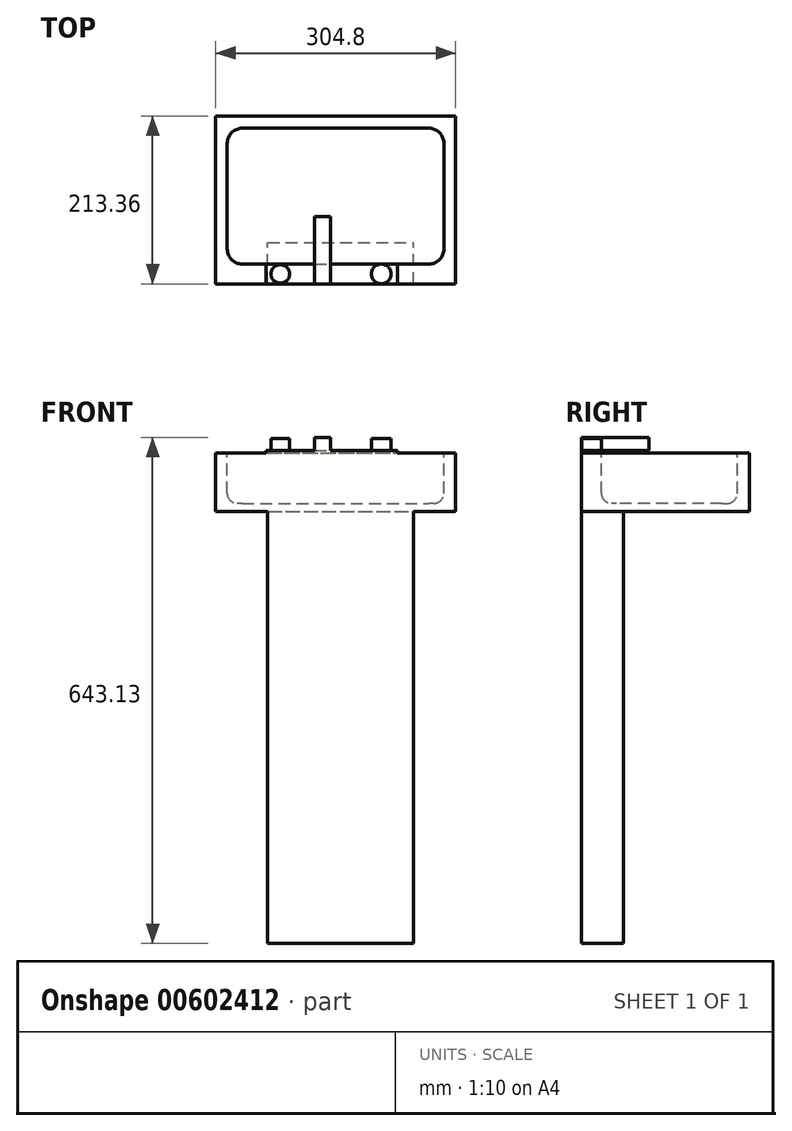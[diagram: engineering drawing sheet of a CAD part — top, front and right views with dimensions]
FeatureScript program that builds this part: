
annotation { "Feature Type Name" : "Feature", "Feature Type Description" : "" }
export const myFeature = defineFeature(function(context is Context, id is Id, definition is map)
    precondition{}
    {
        {
            var Q0;
            Q0=qCreatedBy(makeId("Top.planeOp"),FACE);
            var sketch = newSketch(context, id + "F0", { "sketchPlane" : qUnion([Q0])});
            skLineSegment(sketch, "E0.bottom", {"start": v(0, 0) * mm, "end": v(304.8, 0) * mm});
            skLineSegment(sketch, "E0.top", {"start": v(0, -213.36) * mm, "end": v(304.8, -213.36) * mm});
            skLineSegment(sketch, "E0.left", {"start": v(0, 0) * mm, "end": v(0, -213.36) * mm});
            skLineSegment(sketch, "E0.right", {"start": v(304.8, 0) * mm, "end": v(304.8, -213.36) * mm});
            skSolve(sketch);
        }
        {
            var Q0;
            Q0=makeQuery(id+"F0.imprint","IMPRINT",FACE,{"disambiguationData":[TD([[makeQuery(id+"F0.imprint","IMPRINT",EDGE,{"derivedFrom":sQuery(id+"F0.wireOp",EDGE,"E0.bottom")}),-1.0]])]});
            extrude(context, id + "F1", {"entities" : qUnion([Q0]), "depth" : 74.68 * mm, "offsetDistance" : 30.48 * mm});
        }
        {
            var Q0;
            Q0=makeQuery(id+"F1.opExtrude","CAP_FACE",FACE,{"disambiguationData":[OSD([sQuery(id+"F0.wireOp",EDGE,"E0.bottom"),sQuery(id+"F0.wireOp",EDGE,"E0.top"),sQuery(id+"F0.wireOp",EDGE,"E0.left"),sQuery(id+"F0.wireOp",EDGE,"E0.right")])],"isStart":true});
            var sketch = newSketch(context, id + "F2", { "sketchPlane" : qUnion([Q0])});
            skLineSegment(sketch, "E1.bottom", {"start": v(65.87, 213.36) * mm, "end": v(251.25, 213.36) * mm});
            skLineSegment(sketch, "E1.top", {"start": v(65.87, 160.62) * mm, "end": v(251.25, 160.62) * mm});
            skLineSegment(sketch, "E1.left", {"start": v(65.87, 213.36) * mm, "end": v(65.87, 160.62) * mm});
            skLineSegment(sketch, "E1.right", {"start": v(251.25, 213.36) * mm, "end": v(251.25, 160.62) * mm});
            skSolve(sketch);
        }
        {
            var Q0;
            Q0=makeQuery(id+"F2.imprint","IMPRINT",FACE,{"disambiguationData":[TD([[makeQuery(id+"F2.imprint","IMPRINT",EDGE,{"derivedFrom":sQuery(id+"F2.wireOp",EDGE,"E1.bottom")}),-1.0]])]});
            extrude(context, id + "F3", {"entities" : qUnion([Q0]), "operationType" : NewBodyOperationType.ADD, "depth" : 548.64 * mm, "offsetDistance" : 30.48 * mm});
        }
        {
            var Q0;
            Q0=makeQuery(id+"F1.opExtrude","CAP_FACE",FACE,{"disambiguationData":[OSD([sQuery(id+"F0.wireOp",EDGE,"E0.bottom"),sQuery(id+"F0.wireOp",EDGE,"E0.top"),sQuery(id+"F0.wireOp",EDGE,"E0.left"),sQuery(id+"F0.wireOp",EDGE,"E0.right")])],"isStart":false});
            var sketch = newSketch(context, id + "F4", { "sketchPlane" : qUnion([Q0])});
            skLineSegment(sketch, "E2.bottom", {"start": v(14.56, -15.67) * mm, "end": v(289.73, -15.67) * mm});
            skLineSegment(sketch, "E2.top", {"start": v(14.56, -188.21) * mm, "end": v(289.73, -188.21) * mm});
            skLineSegment(sketch, "E2.left", {"start": v(14.56, -15.67) * mm, "end": v(14.56, -188.21) * mm});
            skLineSegment(sketch, "E2.right", {"start": v(289.73, -15.67) * mm, "end": v(289.73, -188.21) * mm});
            skSolve(sketch);
        }
        {
            var Q0;
            Q0=makeQuery(id+"F4.imprint","IMPRINT",FACE,{"disambiguationData":[TD([[makeQuery(id+"F4.imprint","IMPRINT",EDGE,{"derivedFrom":sQuery(id+"F4.wireOp",EDGE,"E2.bottom")}),-1.0]])]});
            extrude(context, id + "F5", {"entities" : qUnion([Q0]), "operationType" : NewBodyOperationType.REMOVE, "oppositeDirection" : true, "depth" : 64 * mm, "offsetDistance" : 30.48 * mm});
        }
        {
            var Q0;
            Q0=makeQuery(id+"F5.boolean.opBoolean","COPY",EDGE,{"derivedFrom":makeQuery(id+"F5.opExtrude","SWEPT_EDGE",EDGE,{"disambiguationData":[OSD([sQuery(id+"F4.wireOp",EDGE,"E2.top"),sQuery(id+"F4.wireOp",EDGE,"E2.right")])]})});
            var Q1;
            Q1=makeQuery(id+"F5.boolean.opBoolean","COPY",EDGE,{"derivedFrom":makeQuery(id+"F5.opExtrude","SWEPT_EDGE",EDGE,{"disambiguationData":[OSD([sQuery(id+"F4.wireOp",EDGE,"E2.top"),sQuery(id+"F4.wireOp",EDGE,"E2.left")])]})});
            var Q2;
            Q2=makeQuery(id+"F5.boolean.opBoolean","COPY",EDGE,{"derivedFrom":makeQuery(id+"F5.opExtrude","SWEPT_EDGE",EDGE,{"disambiguationData":[OSD([sQuery(id+"F4.wireOp",EDGE,"E2.bottom"),sQuery(id+"F4.wireOp",EDGE,"E2.left")])]})});
            var Q3;
            Q3=makeQuery(id+"F5.boolean.opBoolean","COPY",EDGE,{"derivedFrom":makeQuery(id+"F5.opExtrude","SWEPT_EDGE",EDGE,{"disambiguationData":[OSD([sQuery(id+"F4.wireOp",EDGE,"E2.bottom"),sQuery(id+"F4.wireOp",EDGE,"E2.right")])]})});
            fillet(context, id + "F6", {"entities" : qUnion([Q0, Q1, Q2, Q3]), "radius" : 19.13 * mm, "tangentPropagation" : true, "allowEdgeOverflow" : false});
        }
        {
            var Q0;
            Q0=makeQuery(id+"F5.boolean.opBoolean","COPY",FACE,{"derivedFrom":makeQuery(id+"F5.opExtrude","CAP_FACE",FACE,{"disambiguationData":[OSD([sQuery(id+"F4.wireOp",EDGE,"E2.bottom"),sQuery(id+"F4.wireOp",EDGE,"E2.top"),sQuery(id+"F4.wireOp",EDGE,"E2.left"),sQuery(id+"F4.wireOp",EDGE,"E2.right")])],"isStart":false})});
            fillet(context, id + "F7", {"entities" : qUnion([Q0]), "radius" : 12.5 * mm, "tangentPropagation" : true, "allowEdgeOverflow" : false});
        }
        {
            var Q0;
            Q0=makeQuery(id+"F1.opExtrude","CAP_FACE",FACE,{"disambiguationData":[OSD([sQuery(id+"F0.wireOp",EDGE,"E0.bottom"),sQuery(id+"F0.wireOp",EDGE,"E0.top"),sQuery(id+"F0.wireOp",EDGE,"E0.left"),sQuery(id+"F0.wireOp",EDGE,"E0.right")])],"isStart":false});
            var sketch = newSketch(context, id + "F8", { "sketchPlane" : qUnion([Q0])});
            skLineSegment(sketch, "E3.bottom", {"start": v(63.95, -213.36) * mm, "end": v(230.72, -213.36) * mm});
            skLineSegment(sketch, "E3.top", {"start": v(63.95, -188.21) * mm, "end": v(230.72, -188.21) * mm});
            skLineSegment(sketch, "E3.left", {"start": v(63.95, -213.36) * mm, "end": v(63.95, -188.21) * mm});
            skLineSegment(sketch, "E3.right", {"start": v(230.72, -213.36) * mm, "end": v(230.72, -188.21) * mm});
            skSolve(sketch);
        }
        {
            var Q0;
            Q0=makeQuery(id+"F8.imprint","IMPRINT",FACE,{"disambiguationData":[TD([[makeQuery(id+"F8.imprint","IMPRINT",EDGE,{"derivedFrom":sQuery(id+"F8.wireOp",EDGE,"E3.bottom")}),1.0]])]});
            extrude(context, id + "F9", {"entities" : qUnion([Q0]), "operationType" : NewBodyOperationType.ADD, "depth" : 3.05 * mm, "offsetDistance" : 30.48 * mm});
        }
        {
            var Q0;
            Q0=makeQuery(id+"F9.opExtrude","CAP_FACE",FACE,{"disambiguationData":[OSD([sQuery(id+"F8.wireOp",EDGE,"E3.bottom"),sQuery(id+"F8.wireOp",EDGE,"E3.top"),sQuery(id+"F8.wireOp",EDGE,"E3.left"),sQuery(id+"F8.wireOp",EDGE,"E3.right")])],"isStart":false});
            var sketch = newSketch(context, id + "F10", { "sketchPlane" : qUnion([Q0])});
            skCircle(sketch, "E4", {"center": v(81.9, -200.79) * mm, "radius": 11.78 * mm});
            skPoint(sketch, "E4.centerSnap0", {"position": v(63.95, -200.79) * mm});
            skCircle(sketch, "E5", {"center": v(210.2, -200.79) * mm, "radius": 12.57 * mm});
            skPoint(sketch, "E5.centerSnap0", {"position": v(230.72, -200.79) * mm});
            skSolve(sketch);
        }
        {
            var Q0;
            Q0=makeQuery(id+"F10.imprint","IMPRINT",FACE,{"disambiguationData":[TD([[makeQuery(id+"F10.imprint","IMPRINT",EDGE,{"derivedFrom":sQuery(id+"F10.wireOp",EDGE,"E4")}),1.0]])]});
            var Q1;
            {var subQ0=sQuery(id+"F10.wireOp",EDGE,"E5");var subQ1=makeQuery(id+"F10.imprint","INTERSECT",VERTEX,{"derivedFrom":[makeQuery(id+"F9.opExtrude","CAP_EDGE",EDGE,{"disambiguationData":[OSD([sQuery(id+"F8.wireOp",EDGE,"E3.bottom")])],"isStart":false}),subQ0]});Q1=makeQuery(id+"F10.imprint","IMPRINT",FACE,{"disambiguationData":[TD([[makeQuery(id+"F10.imprint","IMPRINT",EDGE,{"disambiguationData":[TD([[subQ1,1.0]])],"derivedFrom":subQ0}),1.0]])]});}
            extrude(context, id + "F11", {"entities" : qUnion([Q0, Q1]), "operationType" : NewBodyOperationType.ADD, "depth" : 15.24 * mm, "offsetDistance" : 30.48 * mm});
        }
        {
            var Q0;
            {var subQ0=sQuery(id+"F8.wireOp",EDGE,"E3.left");var subQ1=sQuery(id+"F8.wireOp",EDGE,"E3.bottom");var subQ2=sQuery(id+"F8.wireOp",EDGE,"E3.top");var subQ3=makeQuery(id+"F9.opExtrude","CAP_FACE",FACE,{"disambiguationData":[OSD([subQ1,subQ2,subQ0,sQuery(id+"F8.wireOp",EDGE,"E3.right")])],"isStart":false});Q0=makeQuery(id+"F11.boolean.opBoolean","SPLIT",FACE,{"disambiguationData":[TD([makeQuery(id+"F9.opExtrude","SWEPT_FACE",FACE,{"disambiguationData":[OSD([subQ0])]})])],"derivedFrom":subQ3});}
            var sketch = newSketch(context, id + "F12", { "sketchPlane" : qUnion([Q0])});
            skLineSegment(sketch, "E6.bottom", {"start": v(125.53, -213.36) * mm, "end": v(146.05, -213.36) * mm});
            skLineSegment(sketch, "E6.top", {"start": v(125.53, -127.92) * mm, "end": v(146.05, -127.92) * mm});
            skLineSegment(sketch, "E6.left", {"start": v(125.53, -213.36) * mm, "end": v(125.53, -127.92) * mm});
            skLineSegment(sketch, "E6.right", {"start": v(146.05, -213.36) * mm, "end": v(146.05, -127.92) * mm});
            skSolve(sketch);
        }
        {
            var Q0;
            Q0 = qSketchRegion(id + "F12", true);
            extrude(context, id + "F13", {"entities" : qUnion([Q0]), "operationType" : NewBodyOperationType.ADD, "depth" : 16.76 * mm, "offsetDistance" : 30.48 * mm});
        }
    });
